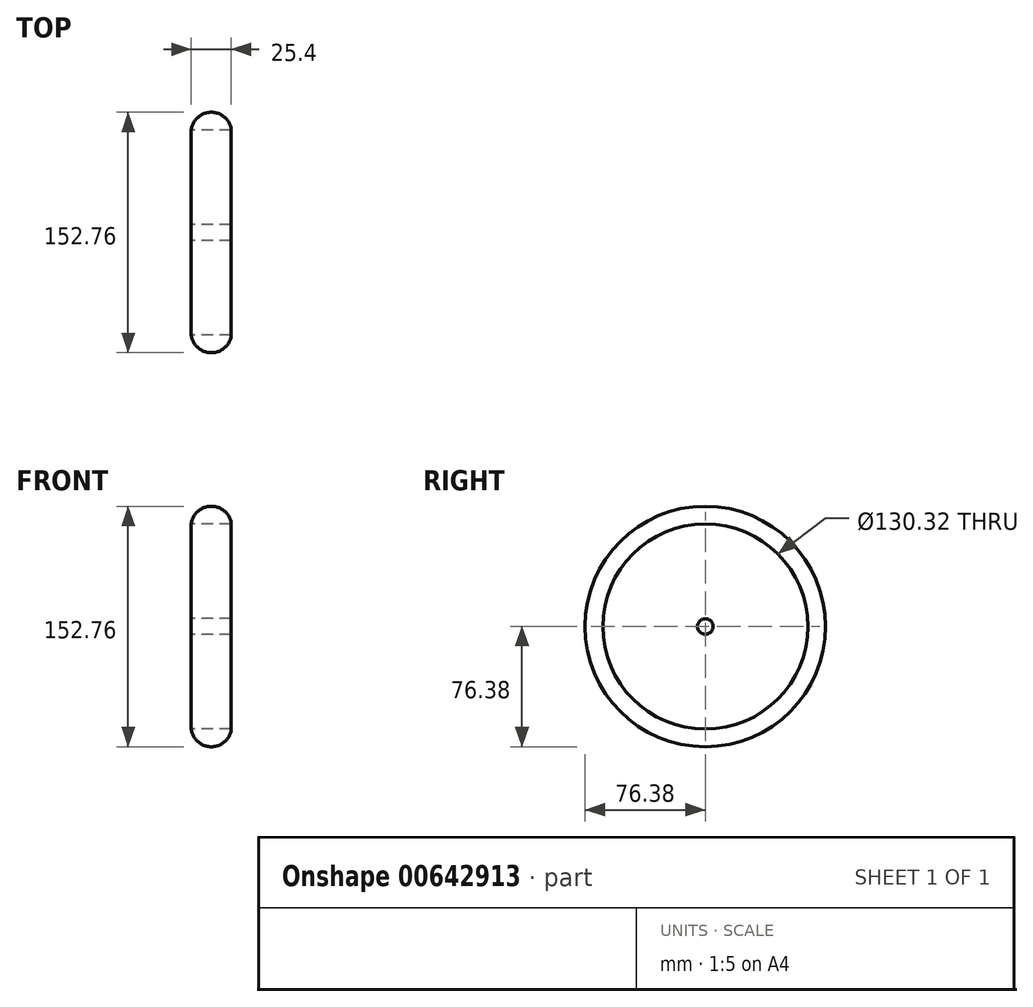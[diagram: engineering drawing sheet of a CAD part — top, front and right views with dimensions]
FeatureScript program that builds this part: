
annotation { "Feature Type Name" : "Feature", "Feature Type Description" : "" }
export const myFeature = defineFeature(function(context is Context, id is Id, definition is map)
    precondition{}
    {
        {
            var Q0;
            Q0=qCreatedBy(makeId("Right.planeOp"),FACE);
            var sketch = newSketch(context, id + "F0", { "sketchPlane" : qUnion([Q0])});
            skCircle(sketch, "E0", {"center": v(0, 0) * mm, "radius": 76.38 * mm});
            skCircle(sketch, "E1", {"center": v(0, 0) * mm, "radius": 65.16 * mm});
            skCircle(sketch, "E2", {"center": v(0, 0) * mm, "radius": 4.97 * mm});
            skArc(sketch, "E3", {"start": v(0, 65.16) * mm, "mid": v(-9.6, 35.06) * mm, "end": v(0, 4.97) * mm});
            skArc(sketch, "E4.1.0", {"start": v(-38.3, 52.72) * mm, "mid": v(-28.37, 22.72) * mm, "end": v(-2.92, 4.02) * mm});
            skArc(sketch, "E4.2.0", {"start": v(-61.97, 20.14) * mm, "mid": v(-36.31, 1.7) * mm, "end": v(-4.72, 1.53) * mm});
            skArc(sketch, "E4.3.0", {"start": v(-61.97, -20.14) * mm, "mid": v(-30.38, -19.96) * mm, "end": v(-4.72, -1.53) * mm});
            skArc(sketch, "E4.4.0", {"start": v(-38.3, -52.72) * mm, "mid": v(-12.84, -34) * mm, "end": v(-2.92, -4.02) * mm});
            skArc(sketch, "E4.5.0", {"start": v(0, -65.16) * mm, "mid": v(9.6, -35.06) * mm, "end": v(0, -4.97) * mm});
            skArc(sketch, "E4.6.0", {"start": v(38.3, -52.72) * mm, "mid": v(28.37, -22.72) * mm, "end": v(2.92, -4.02) * mm});
            skArc(sketch, "E4.7.0", {"start": v(61.97, -20.14) * mm, "mid": v(36.31, -1.7) * mm, "end": v(4.72, -1.53) * mm});
            skArc(sketch, "E4.8.0", {"start": v(61.97, 20.14) * mm, "mid": v(30.38, 19.96) * mm, "end": v(4.72, 1.53) * mm});
            skArc(sketch, "E4.9.0", {"start": v(38.3, 52.72) * mm, "mid": v(12.84, 34) * mm, "end": v(2.92, 4.02) * mm});
            skSolve(sketch);
        }
        {
            var Q0;
            Q0=qCreatedBy(makeId("Right.planeOp"),FACE);
            var sketch = newSketch(context, id + "F1", { "sketchPlane" : qUnion([Q0])});
            skLineSegment(sketch, "E5", {"start": v(0, 5.08) * mm, "end": v(0, 64.07) * mm});
            skLineSegment(sketch, "E6.1.0", {"start": v(-2.99, 4.11) * mm, "end": v(-37.66, 51.83) * mm});
            skLineSegment(sketch, "E6.2.0", {"start": v(-4.83, 1.57) * mm, "end": v(-60.93, 19.8) * mm});
            skLineSegment(sketch, "E6.3.0", {"start": v(-4.83, -1.57) * mm, "end": v(-60.93, -19.8) * mm});
            skLineSegment(sketch, "E6.4.0", {"start": v(-2.99, -4.11) * mm, "end": v(-37.66, -51.83) * mm});
            skLineSegment(sketch, "E6.5.0", {"start": v(0, -5.08) * mm, "end": v(0, -64.07) * mm});
            skLineSegment(sketch, "E6.6.0", {"start": v(2.99, -4.11) * mm, "end": v(37.66, -51.83) * mm});
            skLineSegment(sketch, "E6.7.0", {"start": v(4.83, -1.57) * mm, "end": v(60.93, -19.8) * mm});
            skLineSegment(sketch, "E6.8.0", {"start": v(4.83, 1.57) * mm, "end": v(60.93, 19.8) * mm});
            skLineSegment(sketch, "E6.9.0", {"start": v(2.99, 4.11) * mm, "end": v(37.66, 51.83) * mm});
            skPoint(sketch, "E6.center", {"position": v(0, 0) * mm});
            skSolve(sketch);
        }
        {
            var Q0;
            Q0=sQuery(id+"F0.wireOp",EDGE,"E4.2.0");
            var Q1;
            Q1=sQuery(id+"F1.wireOp",EDGE,"E6.2.0");
            var Q2;
            Q2=sQuery(id+"F0.wireOp",EDGE,"E4.1.0");
            var Q3;
            Q3=sQuery(id+"F1.wireOp",EDGE,"E6.1.0");
            var Q4;
            Q4=sQuery(id+"F0.wireOp",EDGE,"E3");
            var Q5;
            Q5=sQuery(id+"F1.wireOp",EDGE,"E5");
            var Q6;
            Q6=sQuery(id+"F0.wireOp",EDGE,"E4.9.0");
            var Q7;
            Q7=sQuery(id+"F1.wireOp",EDGE,"E6.9.0");
            var Q8;
            Q8=sQuery(id+"F0.wireOp",EDGE,"E4.8.0");
            var Q9;
            Q9=sQuery(id+"F1.wireOp",EDGE,"E6.8.0");
            var Q10;
            Q10=sQuery(id+"F0.wireOp",EDGE,"E4.7.0");
            var Q11;
            Q11=sQuery(id+"F1.wireOp",EDGE,"E6.7.0");
            var Q12;
            Q12=sQuery(id+"F0.wireOp",EDGE,"E4.6.0");
            var Q13;
            Q13=sQuery(id+"F1.wireOp",EDGE,"E6.6.0");
            var Q14;
            Q14=sQuery(id+"F0.wireOp",EDGE,"E4.5.0");
            var Q15;
            Q15=sQuery(id+"F1.wireOp",EDGE,"E6.5.0");
            var Q16;
            Q16=sQuery(id+"F0.wireOp",EDGE,"E4.4.0");
            var Q17;
            Q17=sQuery(id+"F1.wireOp",EDGE,"E6.4.0");
            var Q18;
            Q18=sQuery(id+"F0.wireOp",EDGE,"E4.3.0");
            var Q19;
            Q19=sQuery(id+"F1.wireOp",EDGE,"E6.3.0");
            extrude(context, id + "F2", {"bodyType" : ToolBodyType.SURFACE, "surfaceEntities" : qUnion([Q0, Q1, Q2, Q3, Q4, Q5, Q6, Q7, Q8, Q9, Q10, Q11, Q12, Q13, Q14, Q15, Q16, Q17, Q18, Q19]), "depth" : 25.4 * mm, "offsetDistance" : 25.4 * mm});
        }
        {
            var Q0;
            Q0=makeQuery(id+"F0.imprint","IMPRINT",FACE,{"disambiguationData":[TD([[makeQuery(id+"F0.imprint","IMPRINT",EDGE,{"derivedFrom":sQuery(id+"F0.wireOp",EDGE,"E0")}),1.0]])]});
            extrude(context, id + "F3", {"entities" : qUnion([Q0]), "depth" : 25.4 * mm, "offsetDistance" : 25.4 * mm});
        }
        {
            var Q0;
            {var subQ0=sQuery(id+"F0.wireOp",EDGE,"E2");var subQ5=makeQuery(id+"F0.imprint","INTERSECT",VERTEX,{"derivedFrom":[subQ0,sQuery(id+"F0.wireOp",EDGE,"E4.8.0")]});Q0=makeQuery(id+"F0.imprint","IMPRINT",FACE,{"disambiguationData":[TD([[makeQuery(id+"F0.imprint","IMPRINT",EDGE,{"disambiguationData":[TD([[subQ5,-1.0]])],"derivedFrom":subQ0}),1.0]])]});}
            extrude(context, id + "F4", {"entities" : qUnion([Q0]), "depth" : 25.4 * mm, "offsetDistance" : 25.4 * mm});
        }
        {
            var Q0;
            Q0=makeQuery(id+"F3.opExtrude","CAP_EDGE",EDGE,{"disambiguationData":[OSD([sQuery(id+"F0.wireOp",EDGE,"E0")])],"isStart":false});
            fillet(context, id + "F5", {"entities" : qUnion([Q0]), "radius" : 12.7 * mm, "tangentPropagation" : true, "allowEdgeOverflow" : false});
        }
        {
            var Q0;
            Q0=makeQuery(id+"F3.opExtrude","SWEPT_FACE",FACE,{"disambiguationData":[OSD([sQuery(id+"F0.wireOp",EDGE,"E0")])]});
            fillet(context, id + "F6", {"entities" : qUnion([Q0]), "radius" : 12.7 * mm, "tangentPropagation" : true, "allowEdgeOverflow" : false});
        }
    });
